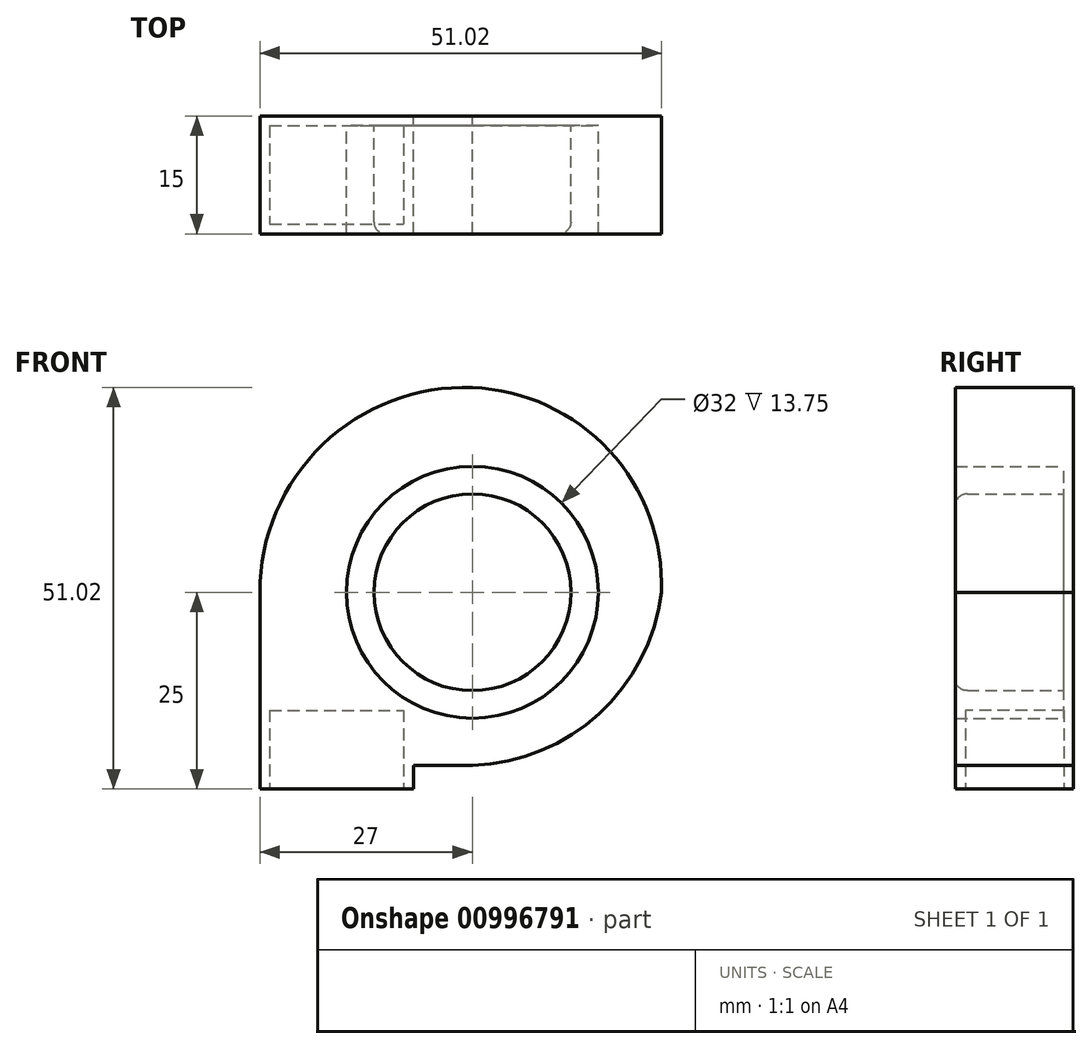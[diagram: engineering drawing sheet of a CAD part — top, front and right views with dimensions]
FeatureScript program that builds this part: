
annotation { "Feature Type Name" : "Feature", "Feature Type Description" : "" }
export const myFeature = defineFeature(function(context is Context, id is Id, definition is map)
    precondition{}
    {
        {
            var Q0;
            Q0=qCreatedBy(makeId("Front.planeOp"),FACE);
            var sketch = newSketch(context, id + "F0", { "sketchPlane" : qUnion([Q0])});
            skLineSegment(sketch, "E0.bottom", {"start": v(0, 0) * mm, "end": v(51, 0) * mm});
            skLineSegment(sketch, "E0.top", {"start": v(0, 51) * mm, "end": v(51, 51) * mm});
            skLineSegment(sketch, "E0.left", {"start": v(0, 0) * mm, "end": v(0, 51) * mm});
            skLineSegment(sketch, "E0.right", {"start": v(51, 0) * mm, "end": v(51, 51) * mm});
            skLineSegment(sketch, "E1", {"start": v(0, 0) * mm, "end": v(19.5, 0) * mm});
            skLineSegment(sketch, "E2", {"start": v(0, 0) * mm, "end": v(0, 25) * mm});
            skLineSegment(sketch, "E3", {"start": v(0, 25) * mm, "end": v(27, 25) * mm, "construction": true});
            skCircle(sketch, "E4", {"center": v(27, 25) * mm, "radius": 16 * mm});
            skCircle(sketch, "E5", {"center": v(27, 25) * mm, "radius": 12.5 * mm});
            skLineSegment(sketch, "E6", {"start": v(27, 25) * mm, "end": v(27, 51) * mm, "construction": true});
            skArc(sketch, "E7", {"start": v(0, 25) * mm, "mid": v(7.97, 43.74) * mm, "end": v(27, 51) * mm});
            skLineSegment(sketch, "E8", {"start": v(27, 25) * mm, "end": v(51, 25) * mm, "construction": true});
            skLineSegment(sketch, "E9", {"start": v(27, 25) * mm, "end": v(27, 0) * mm, "construction": true});
            skLineSegment(sketch, "E10", {"start": v(27, 0) * mm, "end": v(27, 3) * mm});
            skArc(sketch, "E11", {"start": v(51, 25) * mm, "mid": v(44.4, 42.98) * mm, "end": v(27, 51) * mm});
            skArc(sketch, "E12", {"start": v(27, 3) * mm, "mid": v(43.07, 9.56) * mm, "end": v(51, 25) * mm});
            skLineSegment(sketch, "E13", {"start": v(27, 3) * mm, "end": v(19.5, 3) * mm});
            skLineSegment(sketch, "E14", {"start": v(19.5, 3) * mm, "end": v(19.5, 0) * mm});
            skSolve(sketch);
        }
        {
            var Q0;
            Q0=makeQuery(id+"F0.imprint","IMPRINT",FACE,{"disambiguationData":[TD([[makeQuery(id+"F0.imprint","IMPRINT",EDGE,{"derivedFrom":sQuery(id+"F0.wireOp",EDGE,"E4")}),-1.0]])]});
            var Q1;
            Q1=makeQuery(id+"F0.imprint","IMPRINT",FACE,{"disambiguationData":[TD([[makeQuery(id+"F0.imprint","IMPRINT",EDGE,{"derivedFrom":sQuery(id+"F0.wireOp",EDGE,"E5")}),1.0]])]});
            var Q2;
            {var subQ0=sQuery(id+"F0.wireOp",EDGE,"E7");var subQ1=sQuery(id+"F0.wireOp",EDGE,"E0.top");var subQ3=makeQuery(id+"F0.imprint","INTERSECT",VERTEX,{"derivedFrom":[subQ1,subQ0]});Q2=makeQuery(id+"F0.imprint","IMPRINT",FACE,{"disambiguationData":[TD([[makeQuery(id+"F0.imprint","IMPRINT",EDGE,{"disambiguationData":[TD([[subQ3,-1.0]])],"derivedFrom":subQ1}),1.0]])]});}
            var Q3;
            {var subQ0=sQuery(id+"F0.wireOp",EDGE,"E11");var subQ1=sQuery(id+"F0.wireOp",EDGE,"E0.right");var subQ2=makeQuery(id+"F0.imprint","INTERSECT",VERTEX,{"derivedFrom":[subQ1,subQ0]});Q3=makeQuery(id+"F0.imprint","IMPRINT",FACE,{"disambiguationData":[TD([[makeQuery(id+"F0.imprint","IMPRINT",EDGE,{"disambiguationData":[TD([[subQ2,1.0]])],"derivedFrom":subQ1}),-1.0]])]});}
            extrude(context, id + "F1", {"entities" : qUnion([Q0, Q1, Q2, Q3]), "depth" : 15 * mm, "offsetDistance" : 25 * mm});
        }
        {
            var Q0;
            Q0=makeQuery(id+"F0.imprint","IMPRINT",FACE,{"disambiguationData":[TD([[makeQuery(id+"F0.imprint","IMPRINT",EDGE,{"derivedFrom":sQuery(id+"F0.wireOp",EDGE,"E4")}),1.0]])]});
            extrude(context, id + "F2", {"entities" : qUnion([Q0]), "operationType" : NewBodyOperationType.ADD, "depth" : 1.25 * mm, "offsetDistance" : 25 * mm});
        }
        {
            var Q0;
            Q0=makeQuery(id+"F1.opExtrude","SWEPT_FACE",FACE,{"disambiguationData":[OSD([sQuery(id+"F0.wireOp",EDGE,"E0.bottom")])]});
            var sketch = newSketch(context, id + "F3", { "sketchPlane" : qUnion([Q0])});
            skLineSegment(sketch, "E15", {"start": v(0, 0) * mm, "end": v(0, 1.25) * mm});
            skLineSegment(sketch, "E16", {"start": v(0, 1.25) * mm, "end": v(1.25, 1.25) * mm});
            skLineSegment(sketch, "E17.bottom", {"start": v(1.25, 1.25) * mm, "end": v(18.25, 1.25) * mm});
            skLineSegment(sketch, "E17.top", {"start": v(1.25, 13.75) * mm, "end": v(18.25, 13.75) * mm});
            skLineSegment(sketch, "E17.left", {"start": v(1.25, 1.25) * mm, "end": v(1.25, 13.75) * mm});
            skLineSegment(sketch, "E17.right", {"start": v(18.25, 1.25) * mm, "end": v(18.25, 13.75) * mm});
            skSolve(sketch);
        }
        {
            var Q0;
            Q0=makeQuery(id+"F3.imprint","IMPRINT",FACE,{"disambiguationData":[TD([[makeQuery(id+"F3.imprint","IMPRINT",EDGE,{"derivedFrom":sQuery(id+"F3.wireOp",EDGE,"E17.bottom")}),1.0]])]});
            extrude(context, id + "F4", {"entities" : qUnion([Q0]), "operationType" : NewBodyOperationType.REMOVE, "oppositeDirection" : true, "depth" : 10 * mm, "offsetDistance" : 25 * mm});
        }
        {
            var Q0;
            Q0=makeQuery(id+"F1.opExtrude","CAP_EDGE",EDGE,{"disambiguationData":[OSD([sQuery(id+"F0.wireOp",EDGE,"E5")])],"isStart":false});
            fillet(context, id + "F5", {"entities" : qUnion([Q0]), "radius" : 1.5 * mm, "tangentPropagation" : true, "allowEdgeOverflow" : false});
        }
    });
